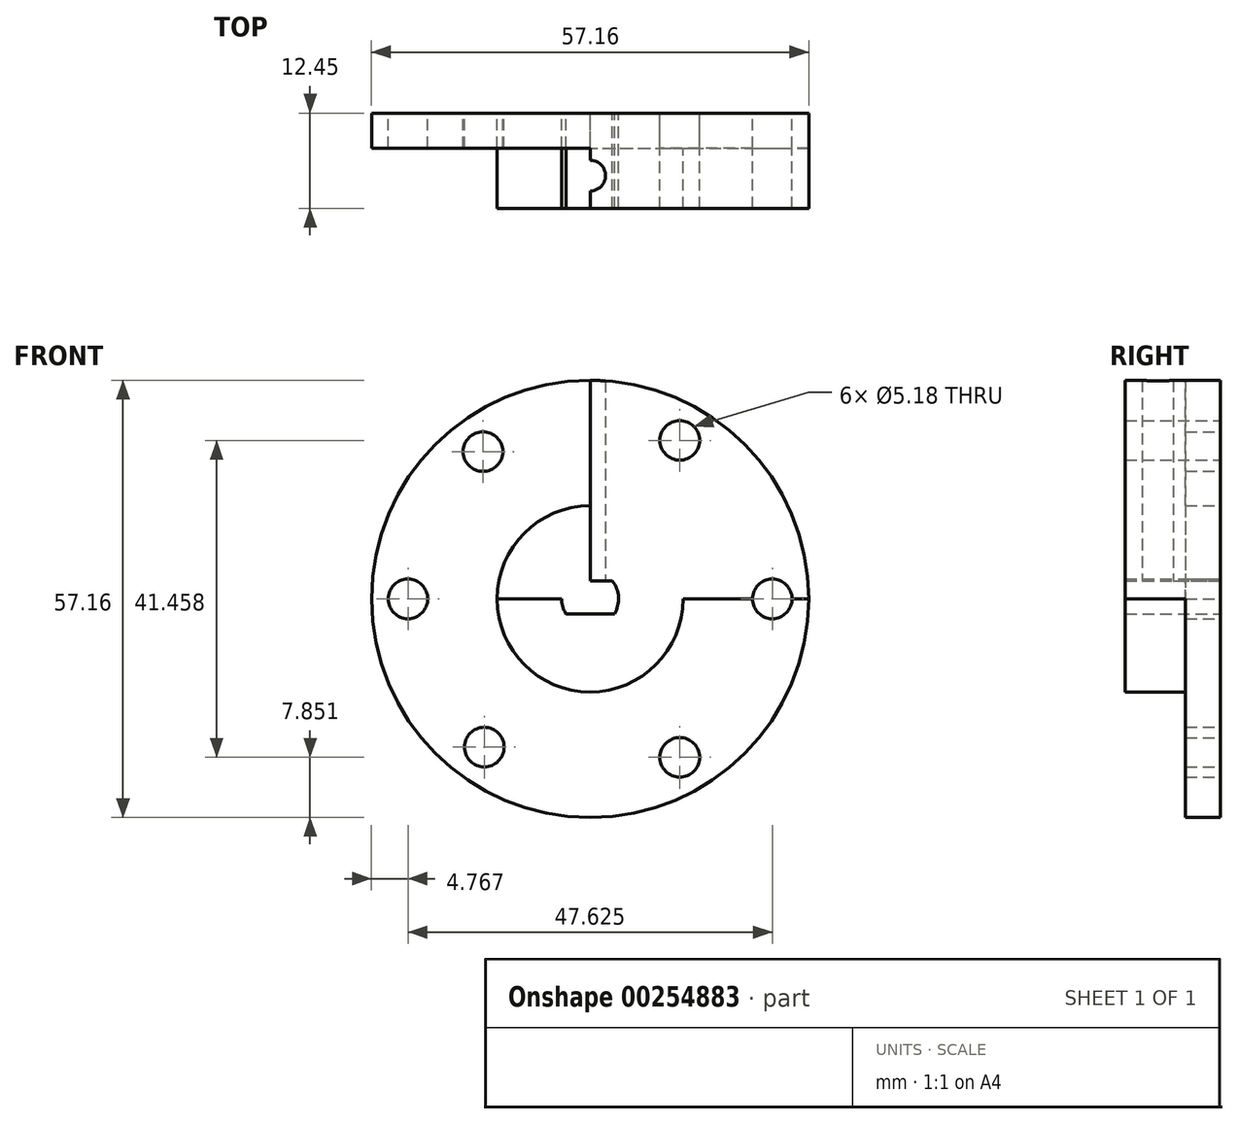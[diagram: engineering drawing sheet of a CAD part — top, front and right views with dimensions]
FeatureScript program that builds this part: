
annotation { "Feature Type Name" : "Feature", "Feature Type Description" : "" }
export const myFeature = defineFeature(function(context is Context, id is Id, definition is map)
    precondition{}
    {
        {
            var Q0;
            Q0=qCreatedBy(makeId("Front.planeOp"),FACE);
            var sketch = newSketch(context, id + "F0", { "sketchPlane" : qUnion([Q0])});
            skCircle(sketch, "E0", {"center": v(0, 0) * mm, "radius": 28.58 * mm});
            skLineSegment(sketch, "E1", {"start": v(-28.58, 0) * mm, "end": v(21.22, 0) * mm});
            skCircle(sketch, "E2", {"center": v(-23.81, 0) * mm, "radius": 2.6 * mm});
            skLineSegment(sketch, "E3", {"start": v(0, 28.58) * mm, "end": v(0, -28.58) * mm});
            skCircle(sketch, "E4", {"center": v(23.81, 0) * mm, "radius": 2.6 * mm});
            skCircle(sketch, "E5", {"center": v(11.72, 20.73) * mm, "radius": 2.6 * mm});
            skCircle(sketch, "E6", {"center": v(-14, 19.26) * mm, "radius": 2.6 * mm});
            skCircle(sketch, "E7", {"center": v(-13.83, -19.38) * mm, "radius": 2.6 * mm});
            skCircle(sketch, "E8", {"center": v(0, 0) * mm, "radius": 12.17 * mm});
            skCircle(sketch, "E9", {"center": v(11.72, -20.73) * mm, "radius": 2.6 * mm});
            skArc(sketch, "E10", {"start": v(-2.92, 2.32) * mm, "mid": v(-3.72, 0.22) * mm, "end": v(-3.17, -1.95) * mm});
            skLineSegment(sketch, "E11", {"start": v(-2.92, 2.32) * mm, "end": v(2.92, 2.32) * mm});
            skLineSegment(sketch, "E12", {"start": v(-3.17, -1.95) * mm, "end": v(3.17, -1.95) * mm});
            skArc(sketch, "E13.trimOffspring", {"start": v(3.17, -1.95) * mm, "mid": v(3.72, 0.22) * mm, "end": v(2.92, 2.32) * mm});
            skLineSegment(sketch, "E14", {"start": v(11.77, 20.73) * mm, "end": v(11.77, 20.7) * mm});
            skLineSegment(sketch, "E15", {"start": v(11.72, 20.73) * mm, "end": v(11.77, 20.73) * mm});
            skLineSegment(sketch, "E16", {"start": v(-23.81, 0) * mm, "end": v(-23.67, 0) * mm});
            skLineSegment(sketch, "E17", {"start": v(-14.08, 19.2) * mm, "end": v(-14.08, 19.16) * mm});
            skLineSegment(sketch, "E18", {"start": v(-14.14, 19.16) * mm, "end": v(-14.08, 19.16) * mm});
            skLineSegment(sketch, "E19", {"start": v(11.82, -20.73) * mm, "end": v(11.82, -20.67) * mm});
            skLineSegment(sketch, "E20", {"start": v(11.82, -20.73) * mm, "end": v(11.72, -20.73) * mm});
            skLineSegment(sketch, "E21", {"start": v(-13.84, -21.97) * mm, "end": v(-13.83, -22.29) * mm});
            skArc(sketch, "E22.trimOffspring", {"start": v(-14, 19.26) * mm, "mid": v(-14.07, 19.21) * mm, "end": v(-14.14, 19.16) * mm});
            skArc(sketch, "E23.trimOffspring", {"start": v(11.77, 20.7) * mm, "mid": v(11.74, 20.71) * mm, "end": v(11.72, 20.73) * mm});
            skArc(sketch, "E24.trimOffspring", {"start": v(11.72, -20.73) * mm, "mid": v(11.77, -20.7) * mm, "end": v(11.82, -20.67) * mm});
            skArc(sketch, "E25.trimOffspring", {"start": v(-13.92, -19.32) * mm, "mid": v(-13.88, -19.35) * mm, "end": v(-13.83, -19.38) * mm});
            skPoint(sketch, "E26.orphan", {"position": v(-14, 16.67) * mm});
            skPoint(sketch, "E27.orphan", {"position": v(-16.6, 19.26) * mm});
            skPoint(sketch, "E28.orphan", {"position": v(-11.42, 19.06) * mm});
            skPoint(sketch, "E29.orphan", {"position": v(14.3, 20.73) * mm});
            skPoint(sketch, "E30.orphan", {"position": v(11.72, 23.32) * mm});
            skPoint(sketch, "E31.orphan", {"position": v(9.13, 20.73) * mm});
            skPoint(sketch, "E32.orphan", {"position": v(11.82, 18.14) * mm});
            skLineSegment(sketch, "E33.trimOffspring", {"start": v(26.4, 0) * mm, "end": v(28.58, 0) * mm});
            skPoint(sketch, "E34.orphan", {"position": v(-26.4, 0) * mm});
            skPoint(sketch, "E35.orphan", {"position": v(-11.42, -20.09) * mm});
            skPoint(sketch, "E36.start.orphan", {"position": v(-16.42, -19.38) * mm});
            skPoint(sketch, "E37.orphan", {"position": v(-14, -16.8) * mm});
            skPoint(sketch, "E38.orphan", {"position": v(14.3, -20.73) * mm});
            skPoint(sketch, "E39.orphan", {"position": v(11.82, -23.32) * mm});
            skLineSegment(sketch, "E40", {"start": v(-1.52, -1.95) * mm, "end": v(-1.52, -12.07) * mm});
            skLineSegment(sketch, "E41", {"start": v(1.48, -1.95) * mm, "end": v(1.48, -12.08) * mm});
            skSolve(sketch);
        }
        {
            var Q0;
            Q0 = qSketchRegion(id + "F0", true);
            extrude(context, id + "F1", {"entities" : qUnion([Q0]), "depth" : 4.57 * mm});
        }
        {
            var Q0;
            {var subQ3=sQuery(id+"F0.wireOp",EDGE,"E40");Q0=makeQuery(id+"F0.imprint","IMPRINT",FACE,{"disambiguationData":[TD([[makeQuery(id+"F0.imprint","IMPRINT",EDGE,{"derivedFrom":subQ3}),-1.0]])]});}
            var Q1;
            {var subQ0=sQuery(id+"F0.wireOp",EDGE,"E41");Q1=makeQuery(id+"F0.imprint","IMPRINT",FACE,{"disambiguationData":[TD([[makeQuery(id+"F0.imprint","IMPRINT",EDGE,{"derivedFrom":subQ0}),1.0]])]});}
            var Q2;
            {var subQ0=sQuery(id+"F0.wireOp",EDGE,"E13.trimOffspring");var subQ7=sQuery(id+"F0.wireOp",EDGE,"E1");var subQ9=makeQuery(id+"F0.imprint","INTERSECT",VERTEX,{"derivedFrom":[subQ7,subQ0]});Q2=makeQuery(id+"F0.imprint","IMPRINT",FACE,{"disambiguationData":[TD([[makeQuery(id+"F0.imprint","IMPRINT",EDGE,{"disambiguationData":[TD([[subQ9,-1.0]])],"derivedFrom":subQ7}),1.0]])]});}
            var Q3;
            {var subQ0=sQuery(id+"F0.wireOp",EDGE,"E8");var subQ1=sQuery(id+"F0.wireOp",EDGE,"E1");var subQ2=makeQuery(id+"F0.imprint","INTERSECT",VERTEX,{"disambiguationData":[OD(0.0)],"derivedFrom":[subQ1,subQ0]});Q3=makeQuery(id+"F0.imprint","IMPRINT",FACE,{"disambiguationData":[TD([[makeQuery(id+"F0.imprint","IMPRINT",EDGE,{"disambiguationData":[TD([[subQ2,-1.0]])],"derivedFrom":subQ1}),1.0]])]});}
            var Q4;
            {var subQ5=sQuery(id+"F0.wireOp",EDGE,"E41");Q4=makeQuery(id+"F0.imprint","IMPRINT",FACE,{"disambiguationData":[TD([[makeQuery(id+"F0.imprint","IMPRINT",EDGE,{"derivedFrom":subQ5}),-1.0]])]});}
            var Q5;
            {var subQ5=sQuery(id+"F0.wireOp",EDGE,"E40");Q5=makeQuery(id+"F0.imprint","IMPRINT",FACE,{"disambiguationData":[TD([[makeQuery(id+"F0.imprint","IMPRINT",EDGE,{"derivedFrom":subQ5}),1.0]])]});}
            extrude(context, id + "F2", {"entities" : qUnion([Q0, Q1, Q2, Q3, Q4, Q5]), "operationType" : NewBodyOperationType.ADD, "depth" : 12.45 * mm});
        }
        {
            var Q0;
            Q0=qCreatedBy(makeId("Top.planeOp"),FACE);
            var sketch = newSketch(context, id + "F3", { "sketchPlane" : qUnion([Q0])});
            skCircle(sketch, "E42", {"center": v(0, -8.18) * mm, "radius": 2.02 * mm});
            skSolve(sketch);
        }
        {
            var Q0;
            Q0 = qSketchRegion(id + "F3", true);
            extrude(context, id + "F4", {"entities" : qUnion([Q0]), "operationType" : NewBodyOperationType.REMOVE, "depth" : 50.8 * mm});
        }
    });
